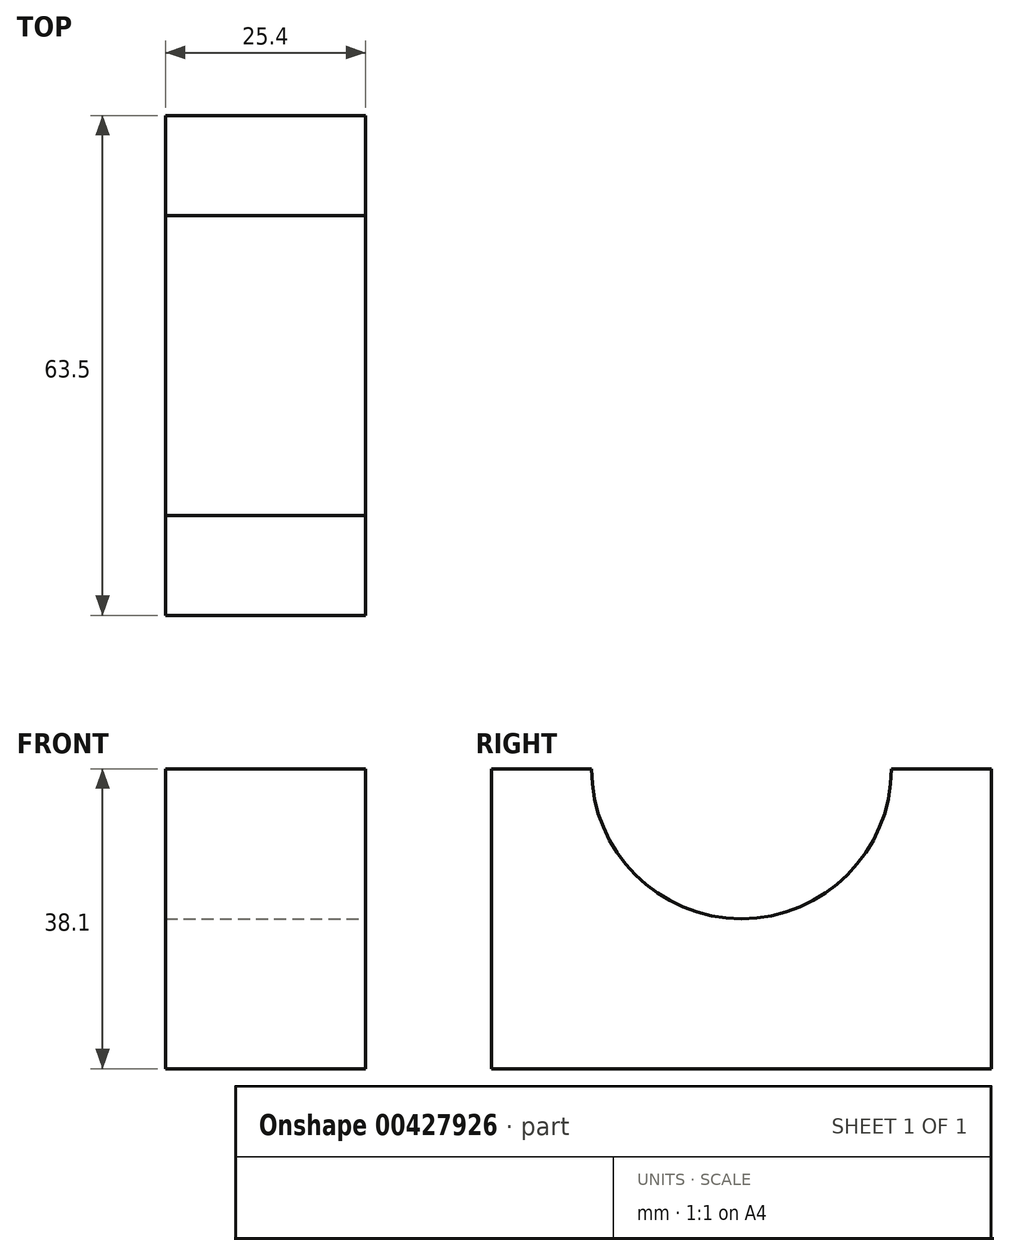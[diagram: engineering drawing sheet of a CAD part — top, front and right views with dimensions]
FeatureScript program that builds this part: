
annotation { "Feature Type Name" : "Feature", "Feature Type Description" : "" }
export const myFeature = defineFeature(function(context is Context, id is Id, definition is map)
    precondition{}
    {
        {
            var Q0;
            Q0=qCreatedBy(makeId("Right.planeOp"),FACE);
            var sketch = newSketch(context, id + "F0", { "sketchPlane" : qUnion([Q0])});
            skLineSegment(sketch, "E0", {"start": v(0, 0) * mm, "end": v(0, 38.1) * mm});
            skLineSegment(sketch, "E1", {"start": v(0, 38.1) * mm, "end": v(63.5, 38.1) * mm});
            skLineSegment(sketch, "E2", {"start": v(63.5, 38.1) * mm, "end": v(63.5, 0) * mm});
            skLineSegment(sketch, "E3", {"start": v(63.5, 0) * mm, "end": v(0, 0) * mm});
            skSolve(sketch);
        }
        {
            var Q0;
            Q0 = qSketchRegion(id + "F0", true);
            extrude(context, id + "F1", {"entities" : qUnion([Q0]), "depth" : 25.4 * mm});
        }
        {
            var Q0;
            Q0=makeQuery(id+"F1.opExtrude","CAP_FACE",FACE,{"disambiguationData":[OSD([sQuery(id+"F0.wireOp",EDGE,"E0"),sQuery(id+"F0.wireOp",EDGE,"E1"),sQuery(id+"F0.wireOp",EDGE,"E2"),sQuery(id+"F0.wireOp",EDGE,"E3")])],"isStart":false});
            var sketch = newSketch(context, id + "F2", { "sketchPlane" : qUnion([Q0])});
            skArc(sketch, "E4", {"start": v(12.7, 38.1) * mm, "mid": v(31.75, 19.05) * mm, "end": v(50.8, 38.1) * mm});
            skSolve(sketch);
        }
        {
            var Q0;
            {var subQ0=sQuery(id+"F2.wireOp",EDGE,"E4");Q0=makeQuery(id+"F2.imprint","IMPRINT",FACE,{"disambiguationData":[TD([[makeQuery(id+"F2.imprint","IMPRINT",EDGE,{"derivedFrom":subQ0}),1.0]])]});}
            extrude(context, id + "F3", {"entities" : qUnion([Q0]), "operationType" : NewBodyOperationType.REMOVE, "oppositeDirection" : true, "depth" : 25.4 * mm});
        }
    });
